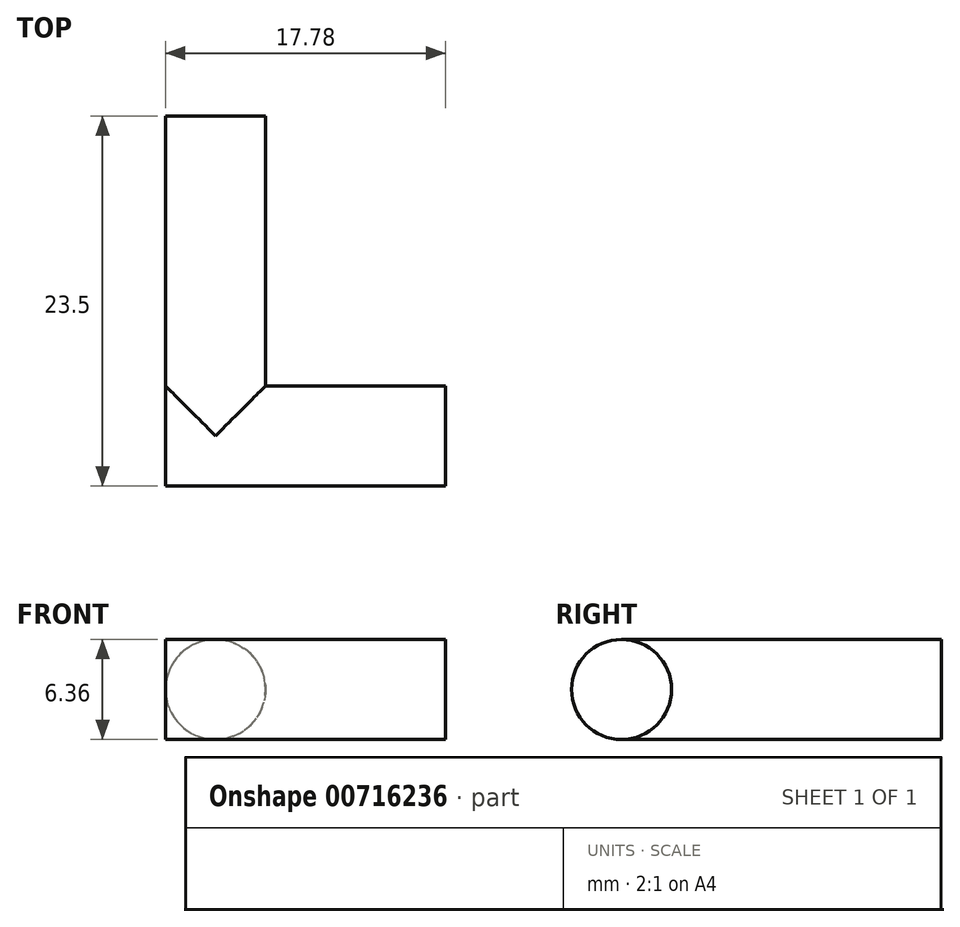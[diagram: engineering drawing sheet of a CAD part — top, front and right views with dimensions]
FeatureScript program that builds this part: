
annotation { "Feature Type Name" : "Feature", "Feature Type Description" : "" }
export const myFeature = defineFeature(function(context is Context, id is Id, definition is map)
    precondition{}
    {
        {
            var Q0;
            Q0=qCreatedBy(makeId("Top.planeOp"),FACE);
            var sketch = newSketch(context, id + "F0", { "sketchPlane" : qUnion([Q0])});
            skLineSegment(sketch, "E0.bottom", {"start": v(-8.15, -3.17) * mm, "end": v(9.63, -3.17) * mm});
            skLineSegment(sketch, "E0.top", {"start": v(-8.15, 0) * mm, "end": v(9.63, 0) * mm});
            skLineSegment(sketch, "E0.left", {"start": v(-8.15, -3.17) * mm, "end": v(-8.15, 0) * mm});
            skLineSegment(sketch, "E0.right", {"start": v(9.63, -3.17) * mm, "end": v(9.63, 0) * mm});
            skSolve(sketch);
        }
        {
            var Q0;
            Q0=qCreatedBy(makeId("Top.planeOp"),FACE);
            var sketch = newSketch(context, id + "F1", { "sketchPlane" : qUnion([Q0])});
            skLineSegment(sketch, "E1.bottom", {"start": v(-8.15, 0) * mm, "end": v(-4.97, 0) * mm});
            skLineSegment(sketch, "E1.top", {"start": v(-8.15, 20.32) * mm, "end": v(-4.97, 20.32) * mm});
            skLineSegment(sketch, "E1.left", {"start": v(-8.15, 0) * mm, "end": v(-8.15, 20.32) * mm});
            skLineSegment(sketch, "E1.right", {"start": v(-4.97, 0) * mm, "end": v(-4.97, 20.32) * mm});
            skSolve(sketch);
        }
        {
            var Q0;
            Q0=makeQuery(id+"F0.imprint","IMPRINT",FACE,{"disambiguationData":[TD([[makeQuery(id+"F0.imprint","IMPRINT",EDGE,{"derivedFrom":sQuery(id+"F0.wireOp",EDGE,"E0.bottom")}),1.0]])]});
            var Q1;
            Q1=sQuery(id+"F0.wireOp",EDGE,"E0.top");
            revolve(context, id + "F2", {"surfaceOperationType" : NewSurfaceOperationType.NEW, "entities" : qUnion([Q0]), "axis" : qUnion([Q1]), "revolveType" : RevolveType.FULL});
        }
        {
            var Q0;
            Q0=makeQuery(id+"F1.imprint","IMPRINT",FACE,{"disambiguationData":[TD([[makeQuery(id+"F1.imprint","IMPRINT",EDGE,{"derivedFrom":sQuery(id+"F1.wireOp",EDGE,"E1.bottom")}),1.0]])]});
            var Q1;
            Q1=sQuery(id+"F1.wireOp",EDGE,"E1.right");
            revolve(context, id + "F3", {"operationType" : NewBodyOperationType.ADD, "surfaceOperationType" : NewSurfaceOperationType.NEW, "entities" : qUnion([Q0]), "axis" : qUnion([Q1]), "revolveType" : RevolveType.FULL});
        }
    });
